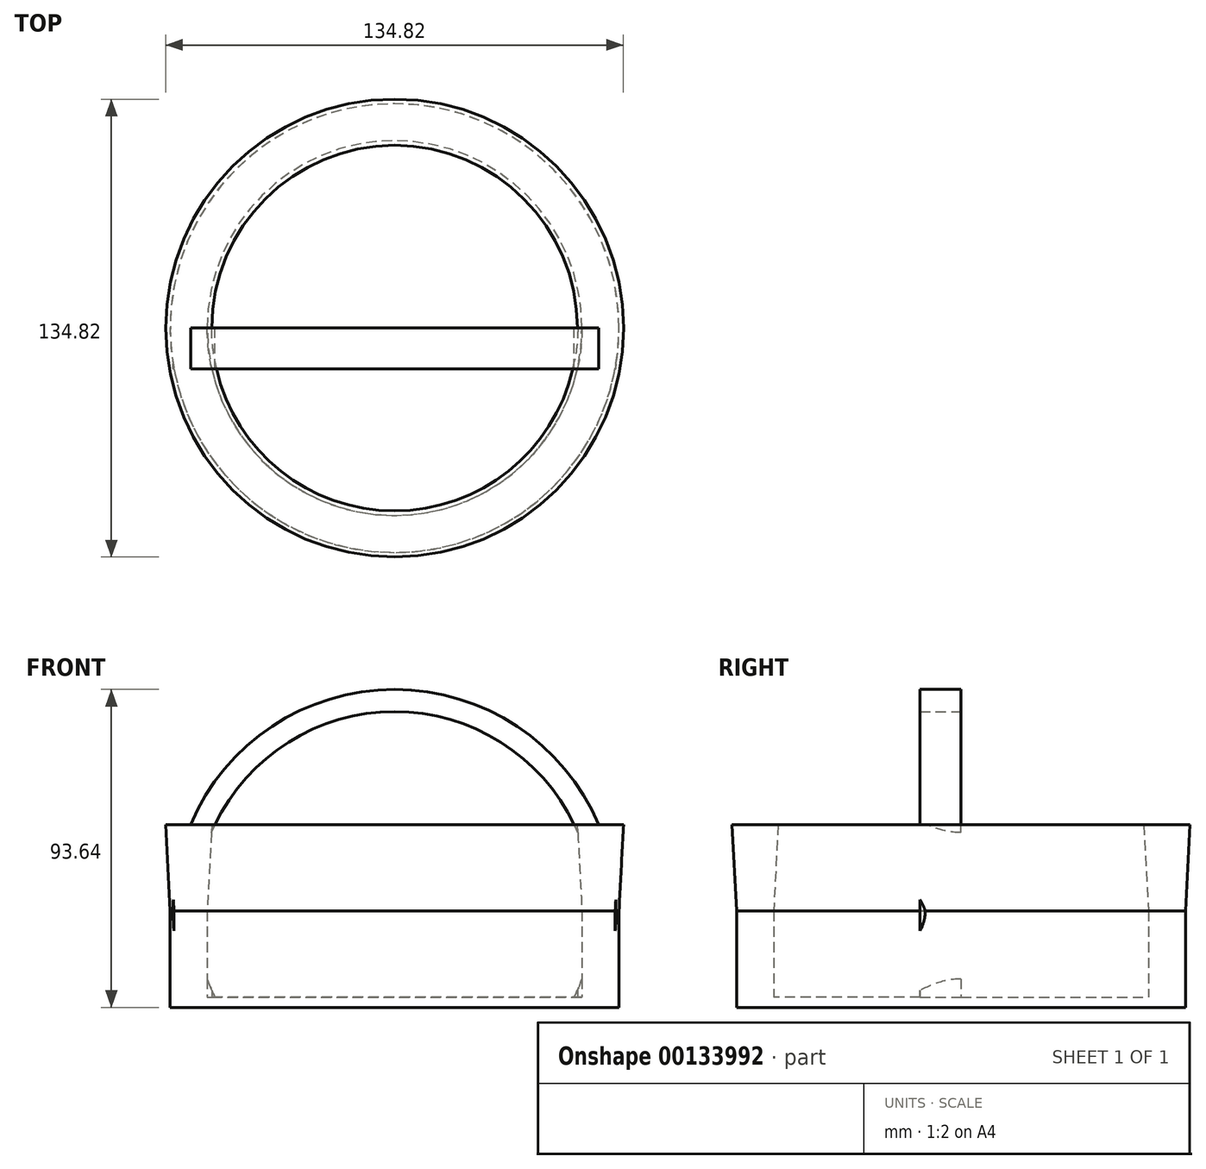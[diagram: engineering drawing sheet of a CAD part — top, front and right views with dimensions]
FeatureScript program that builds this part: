
annotation { "Feature Type Name" : "Feature", "Feature Type Description" : "" }
export const myFeature = defineFeature(function(context is Context, id is Id, definition is map)
    precondition{}
    {
        {
            var Q0;
            Q0=qCreatedBy(makeId("Front.planeOp"),FACE);
            var sketch = newSketch(context, id + "F0", { "sketchPlane" : qUnion([Q0])});
            skCircle(sketch, "E0", {"center": v(0, 0) * mm, "radius": 65.24 * mm});
            skCircle(sketch, "E1", {"center": v(0, 0) * mm, "radius": 58.7 * mm});
            skSolve(sketch);
        }
        {
            var Q0;
            Q0 = qSketchRegion(id + "F0", true);
            extrude(context, id + "F1", {"entities" : qUnion([Q0]), "depth" : 12.06 * mm});
        }
        {
            var Q0;
            Q0=qCreatedBy(makeId("Top.planeOp"),FACE);
            var sketch = newSketch(context, id + "F2", { "sketchPlane" : qUnion([Q0])});
            skCircle(sketch, "E2", {"center": v(0, 0) * mm, "radius": 66.08 * mm});
            skCircle(sketch, "E3.0", {"center": v(0, 0) * mm, "radius": 55.18 * mm});
            skSolve(sketch);
        }
        {
            var Q0;
            Q0=makeQuery(id+"F2.imprint","IMPRINT",FACE,{"disambiguationData":[TD([[makeQuery(id+"F2.imprint","IMPRINT",EDGE,{"derivedFrom":sQuery(id+"F2.wireOp",EDGE,"E2")}),1.0]])]});
            extrude(context, id + "F3", {"entities" : qUnion([Q0]), "operationType" : NewBodyOperationType.ADD, "depth" : 25.4 * mm, "hasDraft" : true, "draftAngle" : 3 * degree, "hasSecondDirection" : true, "secondDirectionOppositeDirection" : true, "secondDirectionDepth" : 25.4 * mm});
        }
        {
            var Q0;
            Q0=qCreatedBy(makeId("Front.planeOp"),FACE);
            var sketch = newSketch(context, id + "F4", { "sketchPlane" : qUnion([Q0])});
            skLineSegment(sketch, "E4.0", {"start": v(-66.08, -25.4) * mm, "end": v(66.08, -25.4) * mm});
            skLineSegment(sketch, "E5", {"start": v(-66.08, -25.4) * mm, "end": v(-61.77, -79.27) * mm});
            skLineSegment(sketch, "E6", {"start": v(-61.77, -79.27) * mm, "end": v(70.85, -79.27) * mm});
            skLineSegment(sketch, "E7", {"start": v(70.85, -79.27) * mm, "end": v(66.08, -25.4) * mm});
            skSolve(sketch);
        }
        {
            var Q0;
            Q0 = qSketchRegion(id + "F4", true);
            extrude(context, id + "F5", {"entities" : qUnion([Q0]), "operationType" : NewBodyOperationType.REMOVE, "depth" : 50.25 * mm});
        }
        {
            var Q0;
            Q0=makeQuery(id+"F5.boolean.opBoolean","MERGE",FACE,{"derivedFrom":[makeQuery(id+"F3.opExtrude","CAP_FACE",FACE,{"disambiguationData":[OSD([sQuery(id+"F2.wireOp",EDGE,"E2"),sQuery(id+"F2.wireOp",EDGE,"E3.0")])],"isStart":true}),makeQuery(id+"F5.opExtrude","SWEPT_FACE",FACE,{"disambiguationData":[OSD([sQuery(id+"F4.wireOp",EDGE,"E4.0")])]})]});
            var sketch = newSketch(context, id + "F6", { "sketchPlane" : qUnion([Q0])});
            skCircle(sketch, "E8.0", {"center": v(0, 0) * mm, "radius": 66.08 * mm});
            skSolve(sketch);
        }
        {
            var Q0;
            Q0 = qSketchRegion(id + "F6", true);
            extrude(context, id + "F7", {"entities" : qUnion([Q0]), "operationType" : NewBodyOperationType.ADD, "depth" : 3 * mm});
        }
    });
